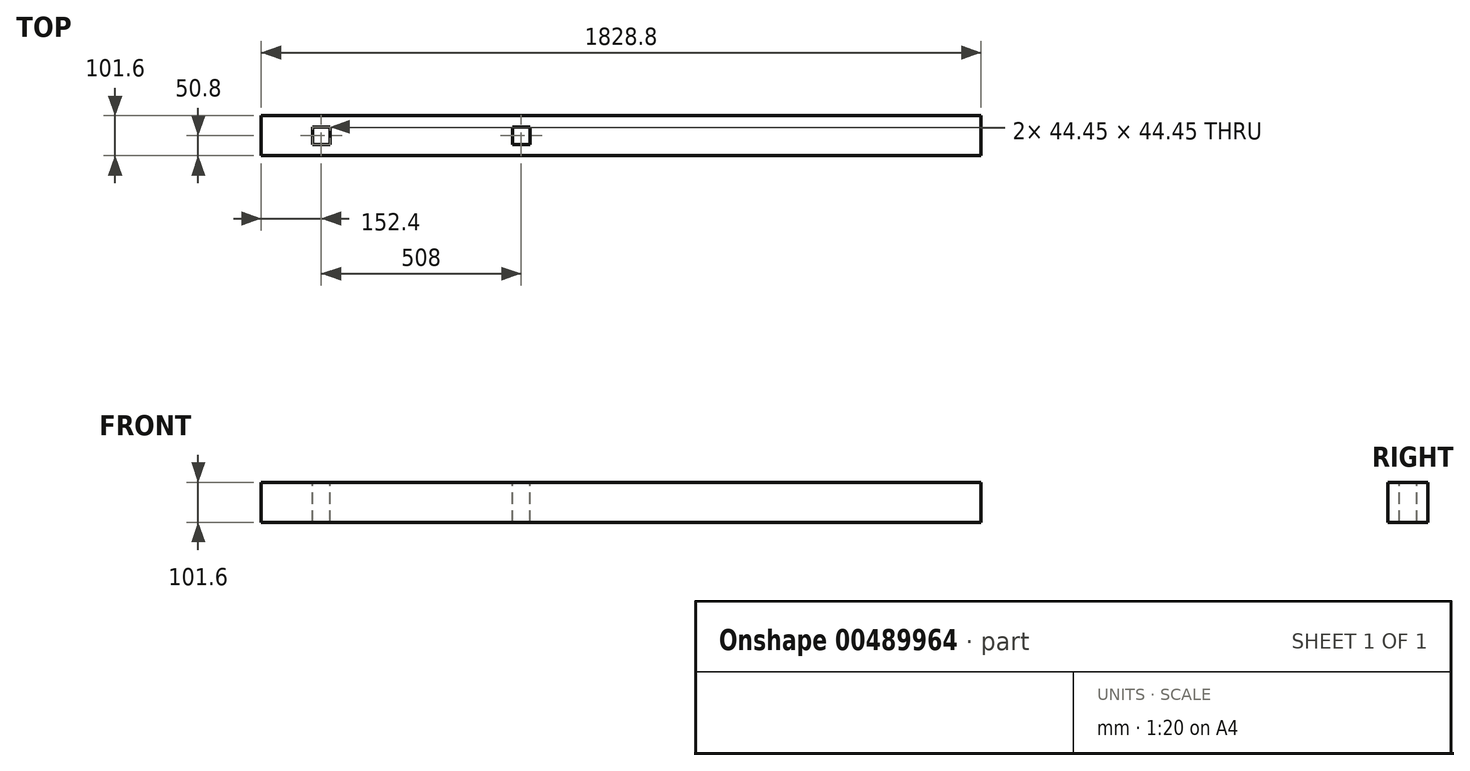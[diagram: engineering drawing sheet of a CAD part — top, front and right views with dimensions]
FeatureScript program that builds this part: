
annotation { "Feature Type Name" : "Feature", "Feature Type Description" : "" }
export const myFeature = defineFeature(function(context is Context, id is Id, definition is map)
    precondition{}
    {
        {
            var Q0;
            Q0=qCreatedBy(makeId("Right.planeOp"),FACE);
            var sketch = newSketch(context, id + "F0", { "sketchPlane" : qUnion([Q0])});
            skLineSegment(sketch, "E0.bottom", {"start": v(-50.8, 50.8) * mm, "end": v(50.8, 50.8) * mm});
            skLineSegment(sketch, "E0.top", {"start": v(-50.8, -50.8) * mm, "end": v(50.8, -50.8) * mm});
            skLineSegment(sketch, "E0.left", {"start": v(-50.8, 50.8) * mm, "end": v(-50.8, -50.8) * mm});
            skLineSegment(sketch, "E0.right", {"start": v(50.8, 50.8) * mm, "end": v(50.8, -50.8) * mm});
            skPoint(sketch, "E0.middle", {"position": v(0, 0) * mm});
            skSolve(sketch);
        }
        {
            var Q0;
            Q0=makeQuery(id+"F0.imprint","IMPRINT",FACE,{"disambiguationData":[TD([[makeQuery(id+"F0.imprint","IMPRINT",EDGE,{"derivedFrom":sQuery(id+"F0.wireOp",EDGE,"E0.bottom")}),-1.0]])]});
            extrude(context, id + "F1", {"entities" : qUnion([Q0]), "endBound" : BoundingType.SYMMETRIC, "depth" : 1828.8 * mm});
        }
        {
            var Q0;
            Q0=makeQuery(id+"F1.opExtrude","SWEPT_FACE",FACE,{"disambiguationData":[OSD([sQuery(id+"F0.wireOp",EDGE,"E0.bottom")])]});
            var sketch = newSketch(context, id + "F2", { "sketchPlane" : qUnion([Q0])});
            skLineSegment(sketch, "E1.bottom", {"start": v(-784.23, 22.22) * mm, "end": v(-739.78, 22.22) * mm});
            skLineSegment(sketch, "E1.top", {"start": v(-784.23, -22.23) * mm, "end": v(-739.78, -22.23) * mm});
            skLineSegment(sketch, "E1.left", {"start": v(-784.23, 22.22) * mm, "end": v(-784.23, -22.23) * mm});
            skLineSegment(sketch, "E1.right", {"start": v(-739.78, 22.22) * mm, "end": v(-739.78, -22.23) * mm});
            skPoint(sketch, "E1.middle", {"position": v(-762, 0) * mm});
            skSolve(sketch);
        }
        {
            var Q0;
            Q0 = qSketchRegion(id + "F2", true);
            extrude(context, id + "F3", {"entities" : qUnion([Q0]), "operationType" : NewBodyOperationType.REMOVE, "endBound" : BoundingType.THROUGH_ALL, "oppositeDirection" : true, "depth" : 25.4 * mm});
        }
        {
            var Q0;
            Q0=makeQuery(id+"F1.opExtrude","SWEPT_FACE",FACE,{"disambiguationData":[OSD([sQuery(id+"F0.wireOp",EDGE,"E0.bottom")])]});
            var sketch = newSketch(context, id + "F4", { "sketchPlane" : qUnion([Q0])});
            skLineSegment(sketch, "E2.bottom", {"start": v(-276.23, 22.23) * mm, "end": v(-231.78, 22.23) * mm});
            skLineSegment(sketch, "E2.top", {"start": v(-276.23, -22.22) * mm, "end": v(-231.78, -22.22) * mm});
            skLineSegment(sketch, "E2.left", {"start": v(-276.23, 22.23) * mm, "end": v(-276.23, -22.22) * mm});
            skLineSegment(sketch, "E2.right", {"start": v(-231.78, 22.23) * mm, "end": v(-231.78, -22.22) * mm});
            skPoint(sketch, "E2.middle", {"position": v(-254, 0) * mm});
            skSolve(sketch);
        }
        {
            var Q0;
            Q0=makeQuery(id+"F4.imprint","IMPRINT",FACE,{"disambiguationData":[TD([[makeQuery(id+"F4.imprint","IMPRINT",EDGE,{"derivedFrom":sQuery(id+"F4.wireOp",EDGE,"E2.bottom")}),-1.0]])]});
            extrude(context, id + "F5", {"entities" : qUnion([Q0]), "operationType" : NewBodyOperationType.REMOVE, "endBound" : BoundingType.THROUGH_ALL, "oppositeDirection" : true, "depth" : 25.4 * mm});
        }
    });
